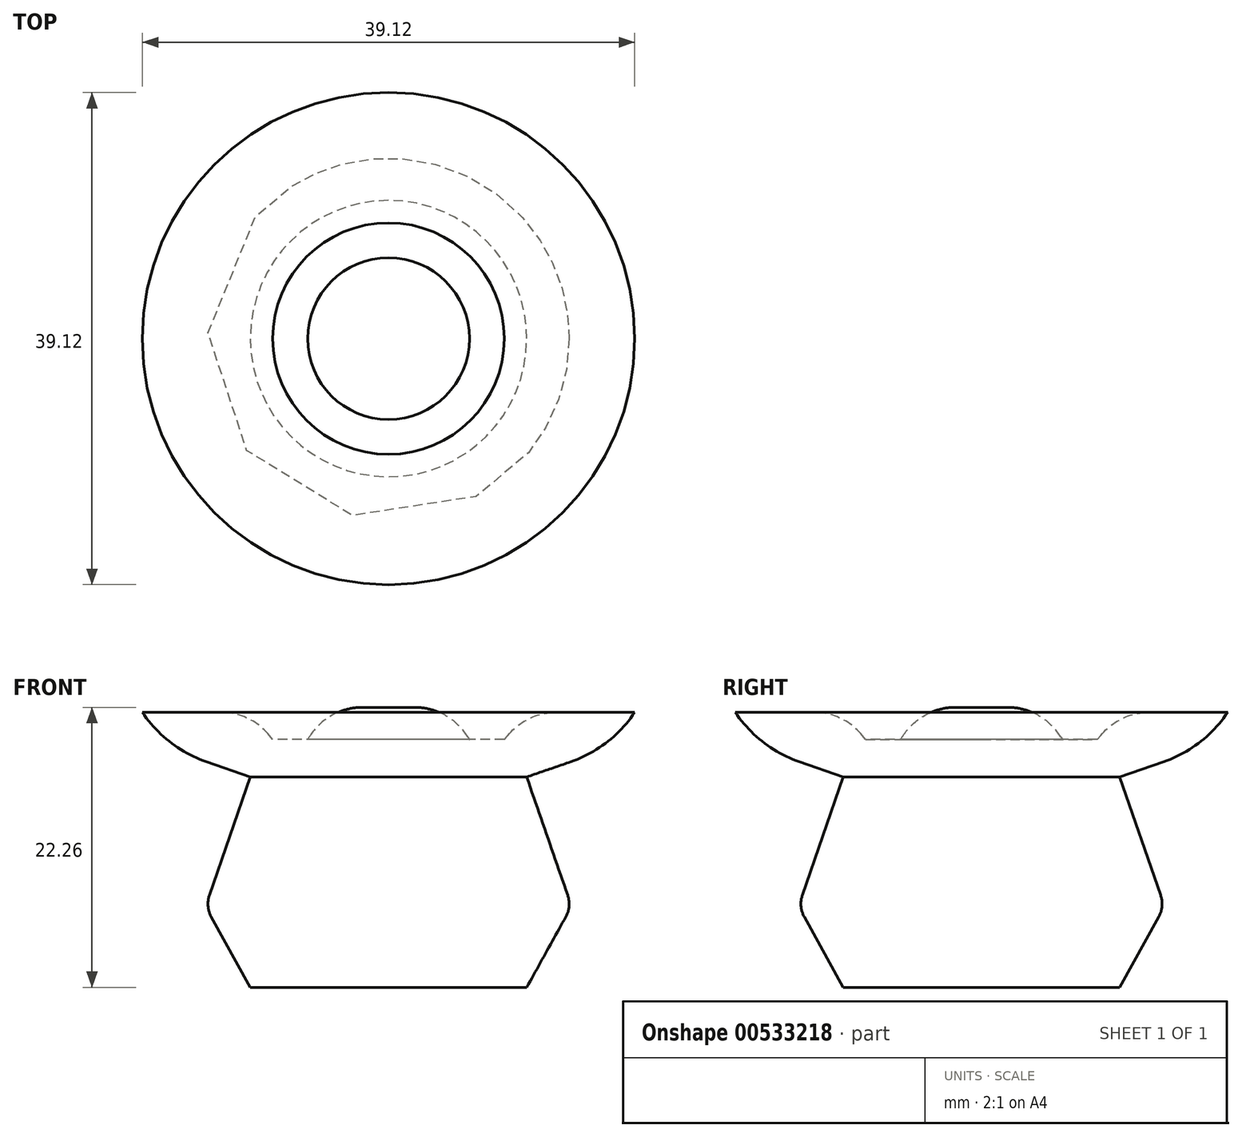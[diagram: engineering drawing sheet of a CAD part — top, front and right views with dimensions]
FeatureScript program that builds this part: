
annotation { "Feature Type Name" : "Feature", "Feature Type Description" : "" }
export const myFeature = defineFeature(function(context is Context, id is Id, definition is map)
    precondition{}
    {
        {
            var Q0;
            Q0=qCreatedBy(makeId("Front.planeOp"),FACE);
            var sketch = newSketch(context, id + "F0", { "sketchPlane" : qUnion([Q0])});
            skLineSegment(sketch, "E0", {"start": v(0, 0) * mm, "end": v(-10.98, 0) * mm});
            skLineSegment(sketch, "E1", {"start": v(-10.98, 0) * mm, "end": v(-14.54, 6.43) * mm});
            skLineSegment(sketch, "E2", {"start": v(-14.54, 6.43) * mm, "end": v(-10.98, 16.72) * mm});
            skLineSegment(sketch, "E3", {"start": v(-10.98, 16.72) * mm, "end": v(-19.56, 19.7) * mm});
            skLineSegment(sketch, "E4", {"start": v(-19.56, 19.7) * mm, "end": v(-19.56, 21.86) * mm});
            skLineSegment(sketch, "E5", {"start": v(-19.56, 21.86) * mm, "end": v(-10.98, 21.86) * mm});
            skLineSegment(sketch, "E6", {"start": v(-10.98, 21.86) * mm, "end": v(-9.2, 19.7) * mm});
            skLineSegment(sketch, "E7", {"start": v(-9.2, 19.7) * mm, "end": v(-6.43, 19.7) * mm});
            skLineSegment(sketch, "E8", {"start": v(-6.43, 19.7) * mm, "end": v(-4.85, 22.26) * mm});
            skLineSegment(sketch, "E9", {"start": v(-4.85, 22.26) * mm, "end": v(0, 22.26) * mm});
            skLineSegment(sketch, "E10", {"start": v(0, 22.26) * mm, "end": v(0, 0) * mm});
            skSolve(sketch);
        }
        {
            var Q0;
            Q0=makeQuery(id+"F0.imprint","IMPRINT",FACE,{"disambiguationData":[TD([[makeQuery(id+"F0.imprint","IMPRINT",EDGE,{"derivedFrom":sQuery(id+"F0.wireOp",EDGE,"E0")}),-1.0]])]});
            var Q1;
            Q1=sQuery(id+"F0.wireOp",EDGE,"E10");
            revolve(context, id + "F1", {"entities" : qUnion([Q0]), "axis" : qUnion([Q1]), "revolveType" : RevolveType.FULL});
        }
        {
            var Q0;
            Q0=makeQuery(id+"F1.opRevolve","SWEPT_EDGE",EDGE,{"disambiguationData":[OSD([sQuery(id+"F0.wireOp",EDGE,"E3"),sQuery(id+"F0.wireOp",EDGE,"E4")])]});
            fillet(context, id + "F2", {"entities" : qUnion([Q0]), "radius" : 10.1 * mm, "tangentPropagation" : true, "allowEdgeOverflow" : false});
        }
        {
            var Q0;
            Q0=makeQuery(id+"F1.opRevolve","SWEPT_EDGE",EDGE,{"disambiguationData":[OSD([sQuery(id+"F0.wireOp",EDGE,"E1"),sQuery(id+"F0.wireOp",EDGE,"E2")])]});
            fillet(context, id + "F3", {"entities" : qUnion([Q0]), "radius" : 2.1 * mm, "tangentPropagation" : true, "allowEdgeOverflow" : false});
        }
        {
            var Q0;
            Q0=makeQuery(id+"F1.opRevolve","SWEPT_EDGE",EDGE,{"disambiguationData":[OSD([sQuery(id+"F0.wireOp",EDGE,"E5"),sQuery(id+"F0.wireOp",EDGE,"E6")])]});
            var Q1;
            Q1=makeQuery(id+"F1.opRevolve","SWEPT_EDGE",EDGE,{"disambiguationData":[OSD([sQuery(id+"F0.wireOp",EDGE,"E8"),sQuery(id+"F0.wireOp",EDGE,"E9")])]});
            fillet(context, id + "F4", {"entities" : qUnion([Q0, Q1]), "radius" : 5 * mm, "tangentPropagation" : true, "allowEdgeOverflow" : false});
        }
    });
